# Revit family: oventrop_hycocon-dtz-1062304-16rfa
name_source: partatom
category: Арматура трубопроводов
revit_build: Autodesk Revit 2017 (Build: 20160225_1515(x64)
units: mm (PartAtom-declared; Revit-internal decimal feet)

## family parameters
Всегда вертикально = Да
Заголовок OmniClass = Adjusting/Controlling Valves for Liquid Services
На основе рабочей плоскости = Нет
Номер OmniClass = 23.65.55.14.17
Общий = Нет
При загрузке вырезать с полостями = Нет
Размер круглого соединителя = Использовать радиус
Тип детали = Клапан - Вставляется

## types (6) — shared parameters
Angle = 55.00°
Article Description = Hycocon DTZ -Differential pressure regulator
Article Type = Hycocon DTZ 10621
Black = Color RGB 35-35-35
Brass = Color RGB 168-128-48
Custom = Нет
EMCS Version = 2.0
ETIM Article Class = EC011463
Family Version = 10.14
IFCExportAs = IfcValveType
IFCExportType = PRESSUREREDUCING
MEPcontent Class = VALVE_BALANCING
Manufacturer URL = http://www.oventrop.de
Pressure Drop = 0.0 Па
Product Line = Oventrop
Rad3 = 13 мм
Rad4 = 15 мм
Rad4_a = 12.43 мм
Rad5 = 10 мм
Revit Version = 2015
Группа модели = Hycocon DTZ 10621
Изготовитель = Oventrop
Описание = Hycocon DTZ -Differential pressure regulator

## per-type parameters (varying)
| type | Bonnet_Diameter | Diameter1 | GTIN | H1 | H2 | H3 | H4 | Height | L1 | Length | Manufacturer Art. No. | NominalDiameter | Nut_Dimension1 | Nut_Dimension2 | OuterDiameter | Rad1 | Rad2 | SW | SW2_UM | Threaded_length | Threaded_length2 | URL |
| DN 15 | 71.5 мм | 26 мм | 4026755263718 | 40 мм | 27.03 мм | 14.13 мм | 2.51 мм | 113 мм | 37.75 мм | 95 мм | 1062304 | 15.00 мм | 27 мм | 30 мм | 21.3 мм | 13 мм | 13.5 мм | 31.18 мм | 34.64 мм | 12.6 мм | 12.6 мм | http://file-system.ru |
| DN 20 | 71.5 мм | 33 мм | 4026755263725 | 40 мм | 30.56 мм | 14.5 мм | 2.58 мм | 116 мм | 42 мм | 98 мм | 1062306 | 20.00 мм | 32 мм | 37 мм | 26.9 мм | 16.5 мм | 16 мм | 36.95 мм | 42.72 мм | 13.7 мм | 13.7 мм | www.stabiplan.com |
| DN 25 | 71.5 мм | 42 мм | 4026755263732 | 45 мм | 36.9 мм | 15 мм | 2.67 мм | 120 мм | 46.25 мм | 105 мм | 1062308 | 25.00 мм | 41 мм | 46 мм | 33.7 мм | 21 мм | 20.5 мм | 47.34 мм | 53.12 мм | 14.8 мм | 14.8 мм | www.stabiplan.com |
| DN 32 | 104 мм | 48 мм | 4026755263749 | 50 мм | 43.24 мм | 17.5 мм | 3.11 мм | 140 мм | 52.2 мм | 129 мм | 1062310 | 32.00 мм | 50 мм | 52 мм | 42.4 мм | 24 мм | 25 мм | 57.74 мм | 60.04 мм | 16.34 мм | 16.34 мм | www.stabiplan.com |
| DN 40 | 104 мм | 54 мм | 4026755263756 | 50 мм | 46.77 мм | 18.13 мм | 3.22 мм | 145 мм | 59 мм | 145 мм | 1062312 | 40.00 мм | 55 мм | 58 мм | 48.3 мм | 27 мм | 27.5 мм | 63.51 мм | 66.97 мм | 18.1 мм | 18.1 мм | www.stabiplan.com |
| DN 50 | 104 мм | 70 мм | 4026755364101 | 65 мм | 57.34 мм | 20.38 мм | 3.62 мм | 163 мм | 67.5 мм | 148 мм | 1062316 | 50.00 мм | 70 мм | 75 мм | 60.3 мм | 35 мм | 35 мм | 80.83 мм | 86.6 мм | 20.3 мм | 20.3 мм | www.stabiplan.com |

## geometry (parser evidence)
native form markers: Sweep x5
no freeform markers — native parametric forms only
